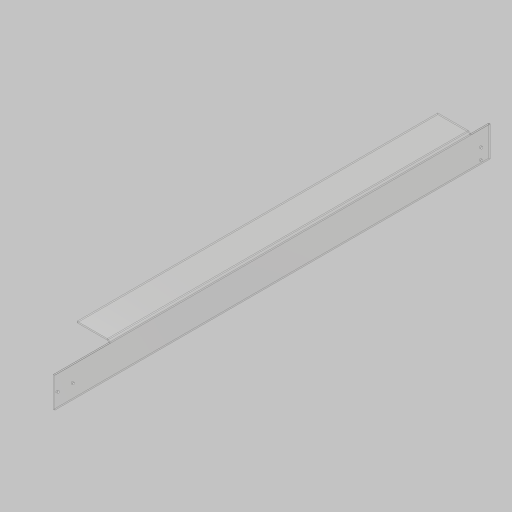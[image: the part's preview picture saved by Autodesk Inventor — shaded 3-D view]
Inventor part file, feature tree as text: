
AUTODESK INVENTOR PART (.ipt)
format: ipt  version: 2023.5 (Build 275446000, 446)  size: 186,368 bytes
history: native  units: in
note: dims shown in document units (in); Inventor stores cm internally (conversion verified against a paired STEP export)
features: sketch x6, sheet_metal_op x5, other x3, hole x2, projected_geometry x1
ambient origin geometry x8: Origin, YZ Plane, XZ Plane, XY Plane, X Axis, Y Axis, Z Axis, Center Point
bodies: Solid1 (feature_tree)
feature tree (17):
  sheet_metal_op  "Face1"
  hole  "Hole1"  [1 undecoded]
  hole  "Hole2"  [1 undecoded]
  sketch  "Sketch5"  dims[d6=0.201in d7=0.75in d8=0.385in d9=0.25in d10=0.5635in d11=0.125in]
  sheet_metal_op  "Face2"
  sheet_metal_op  "Fold3"
  sheet_metal_op  "Fold1"
  sketch  "Sketch1"  dims[d0=2.75in d1=39.375in]
  other  "Plate1"
  sketch  "Sketch2"  dims[d2=0.125in d3=0.3125in]
  sketch  "Sketch3"  dims[d4=1.375in]
  sketch  "Sketch4"  dims[d5=1.5in]
  other  "Plate2"
  sheet_metal_op  "Bend1"
  sketch  "Sketch6"  dims[d12=0.8108in d13=7.5in d14=0.125in d15=0.0625in d16=0.25in d17=0.125in d18=90.0deg d19=0.125in d20=1.0in d21=0.75in d22=0.201in d23=0.38in d24=0.385in d25=0.25in d26=0.5635in d27=0.125in d28=0.8108in d29=1.75in d30=5.0in d31=3.0in d32=0.125in d33=0.125in d34=0.0625in d35=0.25in d36=0.125in d43=0.125in d44=0.125in d45=0.0625in d46=0.25in d47=0.125in d48=90.0deg d49=0.125in d50=1.5in]
  projected_geometry  "Project Cut Edges1"
  other  "Definition1"
note: 2 required parameter values undecoded (feature->parameter linkage not recoverable at this tier; creation-order binding heuristic only, values carry confidence <= 0.55)
